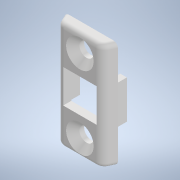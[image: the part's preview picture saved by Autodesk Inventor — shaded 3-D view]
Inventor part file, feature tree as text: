
AUTODESK INVENTOR PART (.ipt)
format: ipt  version: 2022 (Build 260153000, 153)  size: 226,816 bytes
history: native  units: mm
features: reference x6, other x5, extrude x4, projected_geometry x4, sketch x3, fillet x2, chamfer x1
ambient origin geometry x8: Origin, YZ Plane, XZ Plane, XY Plane, X Axis, Y Axis, Z Axis, Center Point
bodies: Body1 (feature_tree)
feature tree (25):
  other  "Твердое тело1"
  extrude  "Выдавливание1"  Depth=0.5mm
  sketch  "Эскиз3"
  other  "РабПлоскость2"
  extrude  "Выдавливание3"  Depth=0.4mm TaperAngle=0.0deg
  extrude  "Выдавливание5"  Depth=0.5mm
  extrude  "Выдавливание6"  Depth=0.25mm
  fillet  "Сопряжение2"  Radius=0.4mm
  fillet  "Сопряжение3"  Radius=0.2mm
  chamfer  "Фаска1"  Distance=2.0mm
  sketch  "Эскиз1"
  projected_geometry  "Спроецированная петля3"
  reference  "Ссылка6"
  projected_geometry  "Спроецированная петля4"
  sketch  "Эскиз6"
  reference  "Ссылка7"
  projected_geometry  "Спроецированная петля5"
  projected_geometry  "Спроецированная петля6"
  reference  "Ссылка8"
  reference  "Ссылка9"
  reference  "Ссылка10"
  reference  "Ссылка11"
  other  "<userpath>\Documents\Git\MZCAT_2024_construction\MZCAT_2024_RPI_2\MZCAT_4.iam"
  other  "MZCAT_4.iam"
  other  "camera fixator:2"
